# Revit family: Shower-Valve_Trim-KOHLER-PARALLEL-K-23496IN-1
name_source: partatom
category: Specialty Equipment
units: mm (PartAtom-declared; Revit-internal decimal feet)

## family parameters
Cut with Voids When Loaded = No
Host = Face
OmniClass Number = 23.31.25.00
Part Type = Normal
Room Calculation Point = No
Round Connector Dimension = Use Diameter
Shared = No

## types (5) — shared parameters
ADA Compliant = No
Assembly Code = C1030200
Date Modified = 08/20/2024
Default Elevation = 42"
Handle Clearance = 3 13/16"
Height = 6 1/2"
Length = 3 3/16"
Manufacturer = Kohler Co.
Master Format 2014 = 10 28 00
Master Format 2014 Name = Toilet, Bath, and Laundry Accessories
Material = Premium Metal Construction
Product Name = PARALLEL
URL = https://www.kohler.co.in
WaterSense Certified = No
Width = 4 1/2"

## per-type parameters (varying)
| type | Description | Finish | Model | Product Page URL | Type |
| CP-Polished Chrome | Recessed Bath & Shower Trim | Kohler-Metal-CP-Polished_Chrome | K-23496IN-4-CP | https://www.kohler.co.in | 1 |
| AF-Vibrant French Gold | Recessed Bath & Shower Trim | Kohler-Metal-AF-Vibrant_French_Gold | K-23496IN-4-AF |  | 2 |
| BN-Vibrant Brushed Nickel | Recessed Bath & Shower Trim | Kohler-Metal-BN-Vibrant_Brushed_Nickel | K-23496IN-4-BN |  | 3 |
| RGD-Polished Rose Gold | Recessed Bath & Shower Trim | Kohler-Metal-RGD-Polished_Rose_Gold | K-23496IN-4-RGD |  | 4 |
| 4SL, BRD-Brushed Rose Gold | AT235 RBS Trim | KOHLER-Metal-BRD-Brushed_Rose_Gold | K-23496IN-4SL-BRD |  | 5 |

## geometry (parser evidence)
native form markers: Sweep x6
no freeform markers — native parametric forms only
